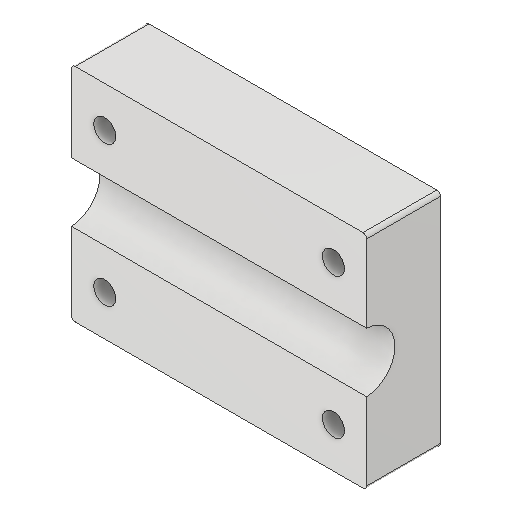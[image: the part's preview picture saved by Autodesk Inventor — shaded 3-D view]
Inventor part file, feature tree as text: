
AUTODESK INVENTOR PART (.ipt)
format: ipt  version: 2025 (Build 290162010, 162A)  size: 167,424 bytes
history: native  units: mm
features: projected_geometry x4, extrude x2, hole x2, sketch x1, fillet x1
ambient origin geometry x8: Origin, YZ Plane, XZ Plane, XY Plane, X Axis, Y Axis, Z Axis, Center Point
bodies: Solid1 (feature_tree)
feature tree (10):
  sketch  "Sketch1"  dims[d1=30.0mm d2=10.0mm d3=0.0mm d20=30.0mm d21=15.0mm d22=0.2mm d23=8.05mm d24=5.0mm d25=0.0mm d26=4.5mm d27=10.979972mm d28=5.489986mm d29=5.489986mm d30=4.5mm d31=3.0mm d32=6.0mm d33=4.0mm d34=2.0mm d35=90.0deg d36=20.0mm d37=20.594885mm d46=0.5mm d47=40.0mm d48=4.25mm d49=4.25mm d50=16.0mm d51=2.5mm d52=6.0mm d53=4.0mm d54=2.0mm d55=90.0deg d56=8.0mm d57=20.594885mm]
  extrude  "Extrusion1"  Depth=10.0mm TaperAngle=0.0deg
  extrude  "Extrusion3"  Depth=30.0mm
  hole  "Hole2"  [1 undecoded]
  fillet  "Fillet2"  Radius=0.2mm
  hole  "Hole4"  [1 undecoded]
  projected_geometry  "Projected Loop1"
  projected_geometry  "Projected Loop2"
  projected_geometry  "Projected Loop3"
  projected_geometry  "Projected Loop6"
note: 2 required parameter values undecoded (feature->parameter linkage not recoverable at this tier; creation-order binding heuristic only, values carry confidence <= 0.55)
